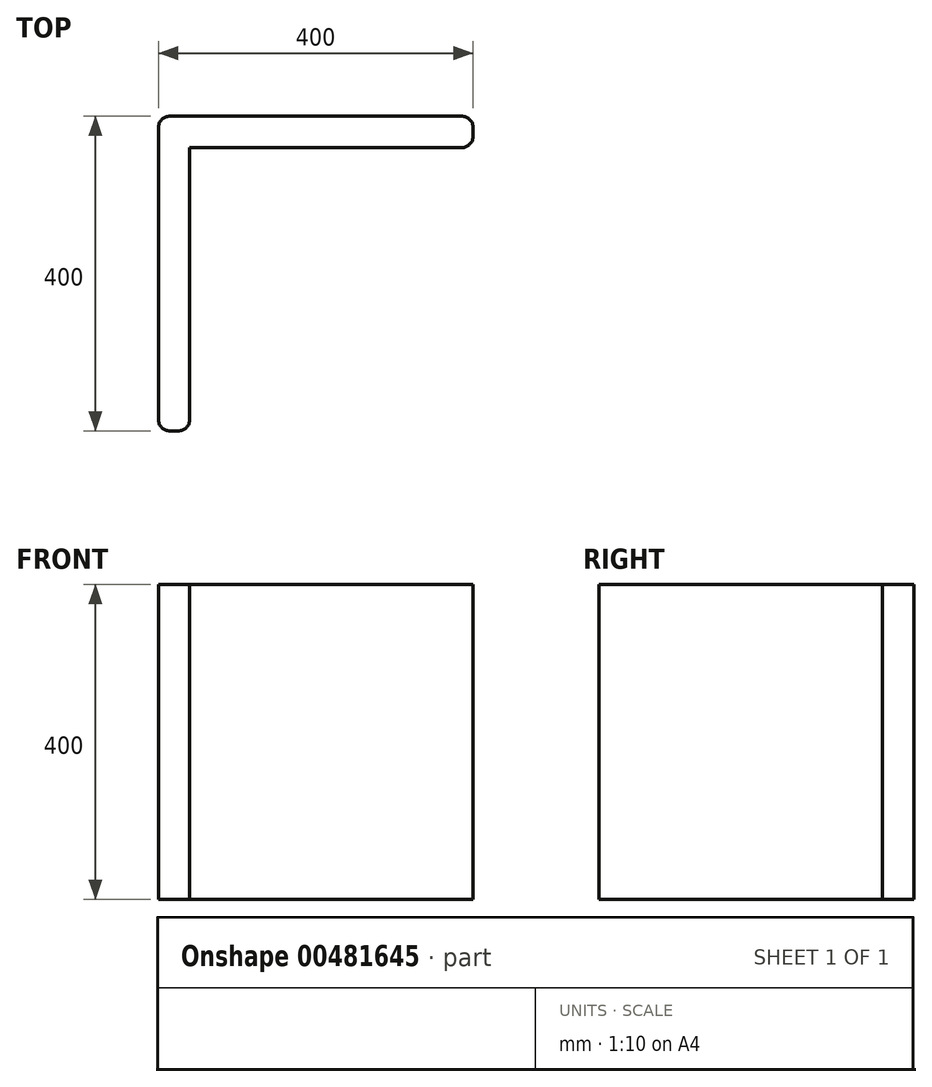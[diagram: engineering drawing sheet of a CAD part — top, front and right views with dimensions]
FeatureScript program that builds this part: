
annotation { "Feature Type Name" : "Feature", "Feature Type Description" : "" }
export const myFeature = defineFeature(function(context is Context, id is Id, definition is map)
    precondition{}
    {
        {
            var Q0;
            Q0=qCreatedBy(makeId("Top.planeOp"),FACE);
            var sketch = newSketch(context, id + "F0", { "sketchPlane" : qUnion([Q0])});
            skLineSegment(sketch, "E0.bottom", {"start": v(0, 0) * mm, "end": v(40, 0) * mm});
            skLineSegment(sketch, "E0.left", {"start": v(0, 0) * mm, "end": v(0, 400) * mm});
            skLineSegment(sketch, "E0.right", {"start": v(40, 0) * mm, "end": v(40, 360) * mm});
            skLineSegment(sketch, "E1.bottom", {"start": v(0, 400) * mm, "end": v(400, 400) * mm});
            skLineSegment(sketch, "E1.top", {"start": v(40, 360) * mm, "end": v(400, 360) * mm});
            skLineSegment(sketch, "E1.right", {"start": v(400, 400) * mm, "end": v(400, 360) * mm});
            skSolve(sketch);
        }
        {
            var Q0;
            Q0 = qSketchRegion(id + "F0", true);
            extrude(context, id + "F1", {"entities" : qUnion([Q0]), "depth" : 400 * mm});
        }
        {
            var Q0;
            Q0=makeQuery(id+"F1.opExtrude","SWEPT_EDGE",EDGE,{"disambiguationData":[OSD([sQuery(id+"F0.wireOp",EDGE,"E0.bottom"),sQuery(id+"F0.wireOp",EDGE,"E0.right")])]});
            var Q1;
            Q1=makeQuery(id+"F1.opExtrude","SWEPT_EDGE",EDGE,{"disambiguationData":[OSD([sQuery(id+"F0.wireOp",EDGE,"E0.bottom"),sQuery(id+"F0.wireOp",EDGE,"E0.left")])]});
            var Q2;
            Q2=makeQuery(id+"F1.opExtrude","SWEPT_EDGE",EDGE,{"disambiguationData":[OSD([sQuery(id+"F0.wireOp",EDGE,"E1.top"),sQuery(id+"F0.wireOp",EDGE,"E1.right")])]});
            var Q3;
            Q3=makeQuery(id+"F1.opExtrude","SWEPT_EDGE",EDGE,{"disambiguationData":[OSD([sQuery(id+"F0.wireOp",EDGE,"E1.bottom"),sQuery(id+"F0.wireOp",EDGE,"E1.right")])]});
            fillet(context, id + "F2", {"entities" : qUnion([Q0, Q1, Q2, Q3]), "radius" : 15 * mm, "tangentPropagation" : true, "allowEdgeOverflow" : false});
        }
        {
            var Q0;
            Q0=makeQuery(id+"F1.opExtrude","SWEPT_EDGE",EDGE,{"disambiguationData":[OSD([sQuery(id+"F0.wireOp",EDGE,"E0.left"),sQuery(id+"F0.wireOp",EDGE,"E1.bottom")])]});
            fillet(context, id + "F3", {"entities" : qUnion([Q0]), "radius" : 15 * mm, "tangentPropagation" : true, "allowEdgeOverflow" : false});
        }
    });
